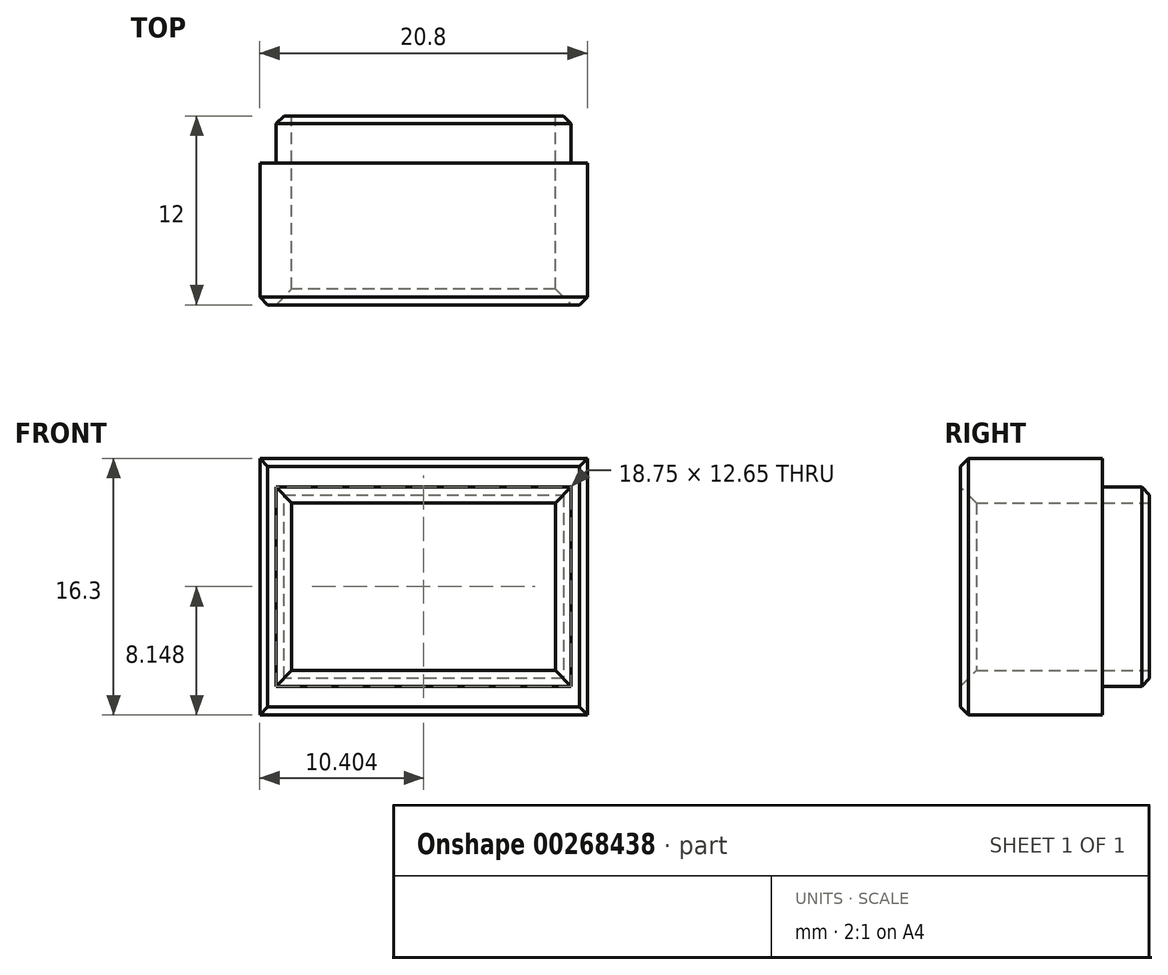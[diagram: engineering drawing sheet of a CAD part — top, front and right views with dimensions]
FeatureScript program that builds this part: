
annotation { "Feature Type Name" : "Feature", "Feature Type Description" : "" }
export const myFeature = defineFeature(function(context is Context, id is Id, definition is map)
    precondition{}
    {
        {
            var Q0;
            Q0=qCreatedBy(makeId("Front.planeOp"),FACE);
            var sketch = newSketch(context, id + "F0", { "sketchPlane" : qUnion([Q0])});
            skLineSegment(sketch, "E0.bottom", {"start": v(-62.38, 34.23) * mm, "end": v(-43.63, 34.23) * mm});
            skLineSegment(sketch, "E0.top", {"start": v(-62.38, 21.58) * mm, "end": v(-43.63, 21.58) * mm});
            skLineSegment(sketch, "E0.left", {"start": v(-62.38, 34.23) * mm, "end": v(-62.38, 21.58) * mm});
            skLineSegment(sketch, "E0.right", {"start": v(-43.63, 34.23) * mm, "end": v(-43.63, 21.58) * mm});
            skLineSegment(sketch, "E1.bottom", {"start": v(-61.38, 33.23) * mm, "end": v(-44.63, 33.23) * mm});
            skLineSegment(sketch, "E1.top", {"start": v(-61.38, 22.58) * mm, "end": v(-44.63, 22.58) * mm});
            skLineSegment(sketch, "E1.left", {"start": v(-61.38, 33.23) * mm, "end": v(-61.38, 22.58) * mm});
            skLineSegment(sketch, "E1.right", {"start": v(-44.63, 33.23) * mm, "end": v(-44.63, 22.58) * mm});
            skSolve(sketch);
        }
        {
            var Q0;
            Q0=makeQuery(id+"F0.imprint","IMPRINT",FACE,{"disambiguationData":[TD([[makeQuery(id+"F0.imprint","IMPRINT",EDGE,{"derivedFrom":sQuery(id+"F0.wireOp",EDGE,"E0.bottom")}),-1.0]])]});
            extrude(context, id + "F1", {"entities" : qUnion([Q0]), "depth" : 3 * mm});
        }
        {
            var Q0;
            Q0=makeQuery(id+"F1.opExtrude","CAP_FACE",FACE,{"disambiguationData":[OSD([sQuery(id+"F0.wireOp",EDGE,"E0.bottom"),sQuery(id+"F0.wireOp",EDGE,"E0.top"),sQuery(id+"F0.wireOp",EDGE,"E0.left"),sQuery(id+"F0.wireOp",EDGE,"E0.right"),sQuery(id+"F0.wireOp",EDGE,"E1.bottom"),sQuery(id+"F0.wireOp",EDGE,"E1.top"),sQuery(id+"F0.wireOp",EDGE,"E1.left"),sQuery(id+"F0.wireOp",EDGE,"E1.right")])],"isStart":false});
            var sketch = newSketch(context, id + "F2", { "sketchPlane" : qUnion([Q0])});
            skLineSegment(sketch, "E2", {"start": v(-62.38, 34.23) * mm, "end": v(-43.63, 21.58) * mm, "construction": true});
            skLineSegment(sketch, "E3", {"start": v(-43.63, 34.23) * mm, "end": v(-62.38, 21.58) * mm, "construction": true});
            skLineSegment(sketch, "E4.bottom", {"start": v(-44.63, 33.23) * mm, "end": v(-61.38, 33.23) * mm});
            skLineSegment(sketch, "E4.top", {"start": v(-44.63, 22.58) * mm, "end": v(-61.38, 22.58) * mm});
            skLineSegment(sketch, "E4.left", {"start": v(-44.63, 33.23) * mm, "end": v(-44.63, 22.58) * mm});
            skLineSegment(sketch, "E4.right", {"start": v(-61.38, 33.23) * mm, "end": v(-61.38, 22.58) * mm});
            skPoint(sketch, "E4.middle", {"position": v(-53, 27.9) * mm});
            skLineSegment(sketch, "E5.bottom", {"start": v(-42.6, 36.06) * mm, "end": v(-63.4, 36.06) * mm});
            skLineSegment(sketch, "E5.top", {"start": v(-42.6, 19.76) * mm, "end": v(-63.4, 19.76) * mm});
            skLineSegment(sketch, "E5.left", {"start": v(-42.6, 36.06) * mm, "end": v(-42.6, 19.76) * mm});
            skLineSegment(sketch, "E5.right", {"start": v(-63.4, 36.06) * mm, "end": v(-63.4, 19.76) * mm});
            skSolve(sketch);
        }
        {
            var Q0;
            Q0=makeQuery(id+"F2.imprint","IMPRINT",FACE,{"disambiguationData":[TD([[makeQuery(id+"F2.imprint","IMPRINT",EDGE,{"derivedFrom":sQuery(id+"F2.wireOp",EDGE,"E4.bottom")}),1.0]])]});
            var Q1;
            Q1=makeQuery(id+"F2.imprint","IMPRINT",FACE,{"disambiguationData":[TD([[makeQuery(id+"F2.imprint","IMPRINT",EDGE,{"derivedFrom":sQuery(id+"F2.wireOp",EDGE,"E5.bottom")}),1.0]])]});
            extrude(context, id + "F3", {"entities" : qUnion([Q0, Q1]), "operationType" : NewBodyOperationType.ADD, "depth" : 9 * mm});
        }
        {
            var Q0;
            Q0=makeQuery(id+"F3.opExtrude","CAP_EDGE",EDGE,{"disambiguationData":[OSD([sQuery(id+"F2.wireOp",EDGE,"E4.bottom")])],"isStart":false});
            var Q1;
            Q1=makeQuery(id+"F3.opExtrude","CAP_EDGE",EDGE,{"disambiguationData":[OSD([sQuery(id+"F2.wireOp",EDGE,"E4.left")])],"isStart":false});
            var Q2;
            Q2=makeQuery(id+"F3.opExtrude","CAP_EDGE",EDGE,{"disambiguationData":[OSD([sQuery(id+"F2.wireOp",EDGE,"E4.top")])],"isStart":false});
            var Q3;
            Q3=makeQuery(id+"F3.opExtrude","CAP_EDGE",EDGE,{"disambiguationData":[OSD([sQuery(id+"F2.wireOp",EDGE,"E4.right")])],"isStart":false});
            chamfer(context, id + "F4", {"entities" : qUnion([Q0, Q1, Q2, Q3]), "width" : 1 * mm, "tangentPropagation" : true});
        }
        {
            var Q0;
            Q0=makeQuery(id+"F1.opExtrude","CAP_EDGE",EDGE,{"disambiguationData":[OSD([sQuery(id+"F0.wireOp",EDGE,"E0.bottom")])],"isStart":true});
            var Q1;
            Q1=makeQuery(id+"F1.opExtrude","CAP_EDGE",EDGE,{"disambiguationData":[OSD([sQuery(id+"F0.wireOp",EDGE,"E0.left")])],"isStart":true});
            var Q2;
            Q2=makeQuery(id+"F1.opExtrude","CAP_EDGE",EDGE,{"disambiguationData":[OSD([sQuery(id+"F0.wireOp",EDGE,"E0.top")])],"isStart":true});
            var Q3;
            Q3=makeQuery(id+"F1.opExtrude","CAP_EDGE",EDGE,{"disambiguationData":[OSD([sQuery(id+"F0.wireOp",EDGE,"E0.right")])],"isStart":true});
            var Q4;
            Q4=makeQuery(id+"F3.opExtrude","CAP_EDGE",EDGE,{"disambiguationData":[OSD([sQuery(id+"F2.wireOp",EDGE,"E5.bottom")])],"isStart":false});
            var Q5;
            Q5=makeQuery(id+"F3.opExtrude","CAP_EDGE",EDGE,{"disambiguationData":[OSD([sQuery(id+"F2.wireOp",EDGE,"E5.right")])],"isStart":false});
            var Q6;
            Q6=makeQuery(id+"F3.opExtrude","CAP_EDGE",EDGE,{"disambiguationData":[OSD([sQuery(id+"F2.wireOp",EDGE,"E5.top")])],"isStart":false});
            var Q7;
            Q7=makeQuery(id+"F3.opExtrude","CAP_EDGE",EDGE,{"disambiguationData":[OSD([sQuery(id+"F2.wireOp",EDGE,"E5.left")])],"isStart":false});
            chamfer(context, id + "F5", {"entities" : qUnion([Q0, Q1, Q2, Q3, Q4, Q5, Q6, Q7]), "width" : 0.5 * mm, "tangentPropagation" : true});
        }
    });
